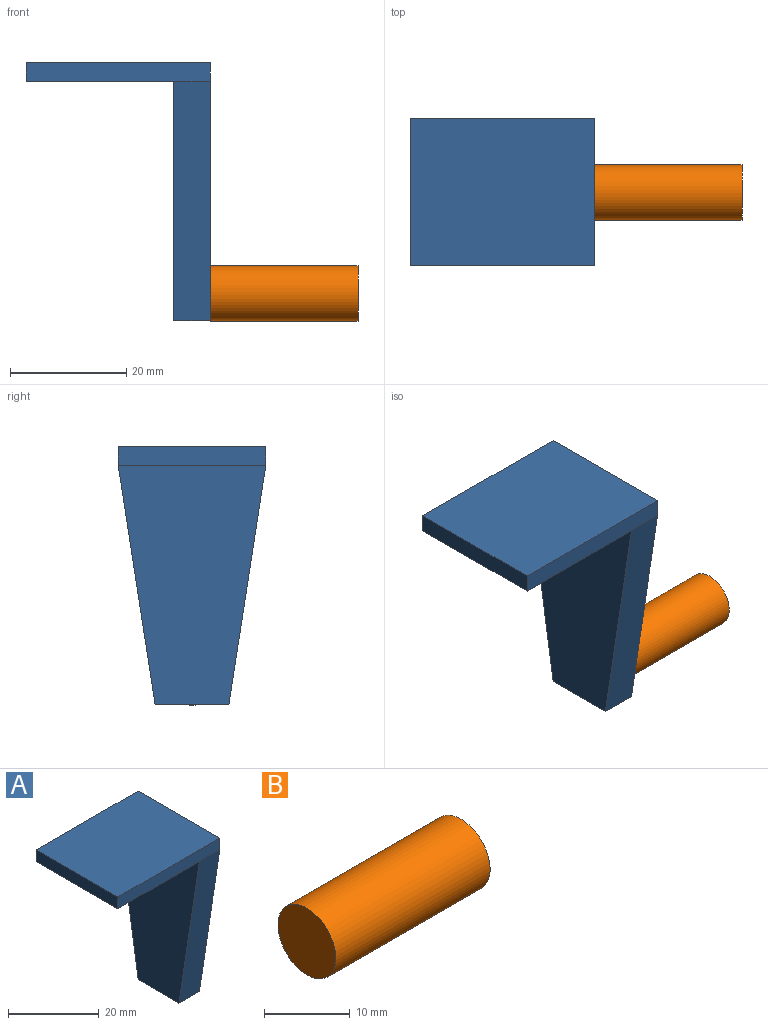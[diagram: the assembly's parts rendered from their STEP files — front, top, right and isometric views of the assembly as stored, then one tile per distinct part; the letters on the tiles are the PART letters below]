
ASSEMBLY  parts=2 mates=1
PART A: 10 faces, bbox 31.8x25.4x44.5 mm
  f0: plane 25.4x25.4mm, normal (0,0,-1), area 645.2mm2, adj f1,f2,f3,f9
  f1: plane 31.75x3.18mm, normal (0,1,0), area 100.8mm2, adj f0,f2,f4,f5,f7
  f2: plane 25.4x3.18mm, normal (-1,0,0), area 80.6mm2, adj f0,f1,f3,f5
  f3: plane 31.75x3.18mm, normal (0,-1,0), area 100.8mm2, adj f0,f2,f4,f5,f8
  f4: plane 44.45x25.4mm, normal (1,0,0), area 866.9mm2, adj f1,f3,f5,f6,f7,f8
  f5: plane 31.75x25.4mm, normal (0,0,1), area 806.5mm2, adj f1,f2,f3,f4
  f6: plane 12.7x6.35mm, normal (0,0,-1), area 80.6mm2, adj f4,f7,f8,f9
  f7: plane 41.28x6.35mm, normal (0,0.99,-0.15), area 265.2mm2, adj f1,f4,f6,f9
  f8: plane 41.28x6.35mm, normal (0,-0.99,-0.15), area 265.2mm2, adj f3,f4,f6,f9
  f9: plane 41.28x25.4mm, normal (-1,0,0), area 786.3mm2, adj f0,f6,f7,f8
PART B: 3 faces, bbox 25.4x9.5x9.5 mm
  f0: cylinder r=4.76mm len=25.4mm, axis (-1,0,0), area 760.1mm2, adj f1,f2
  f1: plane 9.53x9.53mm, normal (1,0,0), area 71.3mm2, adj f0
  f2: plane 9.53x9.53mm, normal (-1,0,0), area 71.3mm2, adj f0
PLACE A t=(26.88,8.55,9.15)mm
PLACE B t=(26.88,8.55,9.1)mm
MATE fastened A.f4 <-> B.f0  axis (1,0,0) through (26.88,8.55,-27.41)mm
